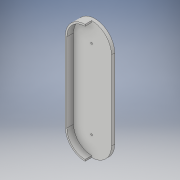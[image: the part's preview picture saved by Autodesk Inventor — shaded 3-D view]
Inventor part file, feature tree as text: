
AUTODESK INVENTOR PART (.ipt)
format: ipt  version: 2017 (Build 210142000, 142)  size: 121,856 bytes
history: native  units: in
note: dims shown in document units (in); Inventor stores cm internally (conversion verified against a paired STEP export)
features: sketch x3, extrude x3
ambient origin geometry x8: Origin, YZ Plane, XZ Plane, XY Plane, X Axis, Y Axis, Z Axis, Center Point
bodies: Solid1 (feature_tree)
feature tree (6):
  sketch  "Sketch1"  dims[d3=0.25in d4=0.0in d17=0.125in]
  extrude  "Extrusion1"  Depth=0.125in
  extrude  "Extrusion4"  Depth=0.5in TaperAngle=0.0deg
  extrude  "Extrusion5"  Depth=0.125in
  sketch  "Sketch4"  dims[d21=0.125in d23=0.125in d24=0.125in d25=0.5in d26=0.0in]
  sketch  "Sketch3"  dims[d18=0.125in d19=0.5in d20=0.0in]
